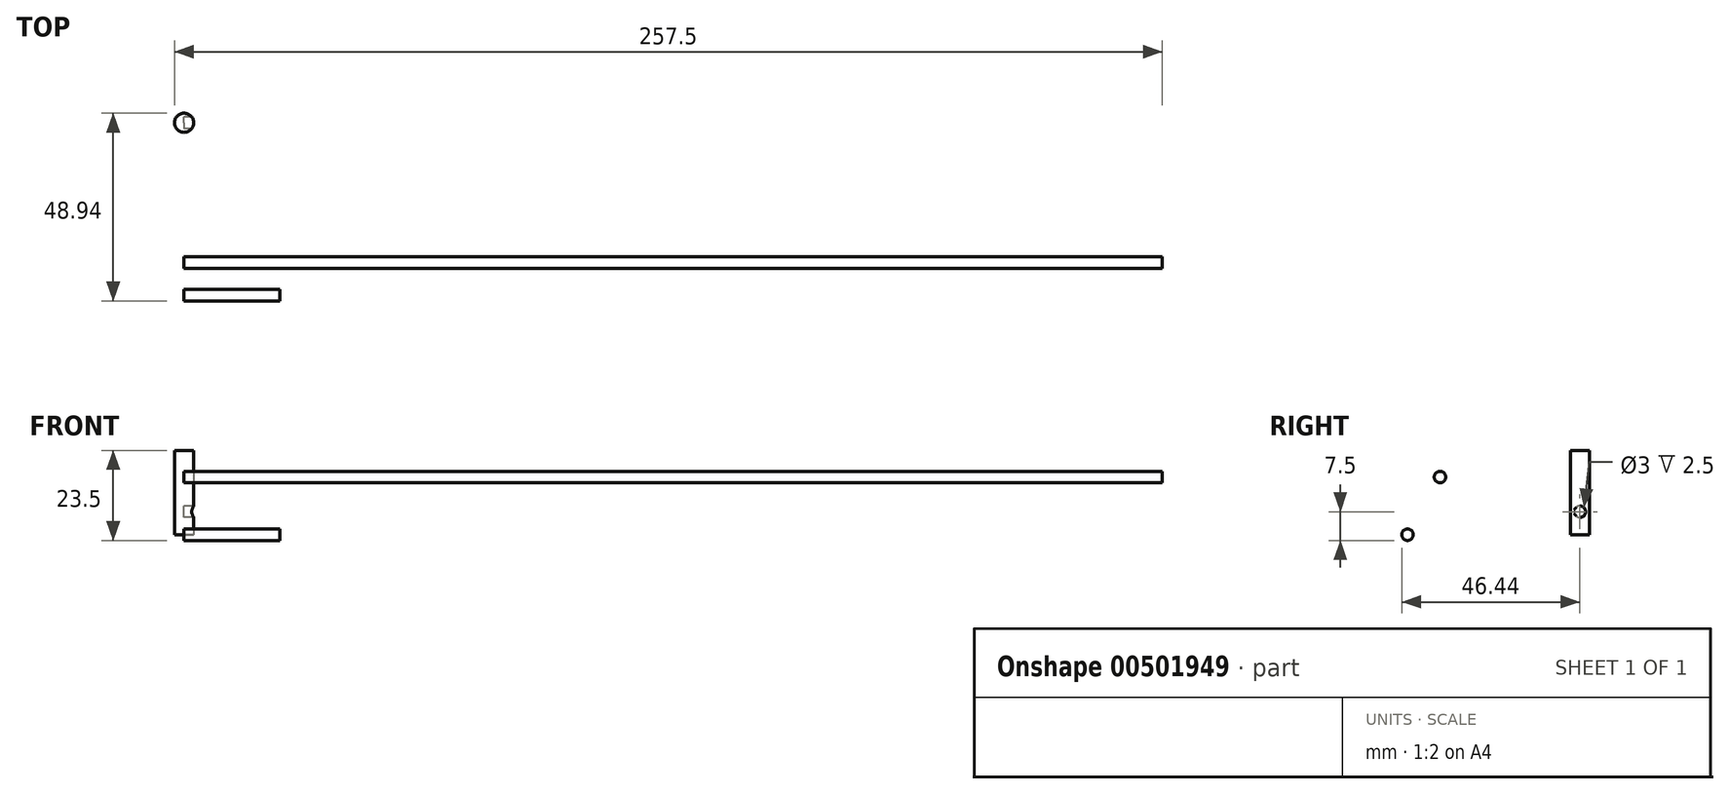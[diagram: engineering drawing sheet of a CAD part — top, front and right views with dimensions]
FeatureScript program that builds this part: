
annotation { "Feature Type Name" : "Feature", "Feature Type Description" : "" }
export const myFeature = defineFeature(function(context is Context, id is Id, definition is map)
    precondition{}
    {
        {
            var Q0;
            Q0=qCreatedBy(makeId("Top.planeOp"),FACE);
            var sketch = newSketch(context, id + "F0", { "sketchPlane" : qUnion([Q0])});
            skCircle(sketch, "E0", {"center": v(0, 0) * mm, "radius": 2.5 * mm});
            skSolve(sketch);
        }
        {
            var Q0;
            Q0 = qSketchRegion(id + "F0", true);
            extrude(context, id + "F1", {"entities" : qUnion([Q0]), "depth" : 22 * mm});
        }
        {
            var Q0;
            Q0=qCreatedBy(makeId("Right.planeOp"),FACE);
            var sketch = newSketch(context, id + "F2", { "sketchPlane" : qUnion([Q0])});
            skCircle(sketch, "E1", {"center": v(0, 6) * mm, "radius": 1.5 * mm});
            skSolve(sketch);
        }
        {
            var Q0;
            Q0 = qSketchRegion(id + "F2", true);
            extrude(context, id + "F3", {"entities" : qUnion([Q0]), "operationType" : NewBodyOperationType.REMOVE, "depth" : 25 * mm});
        }
        {
            var Q0;
            Q0=qCreatedBy(makeId("Right.planeOp"),FACE);
            var sketch = newSketch(context, id + "F4", { "sketchPlane" : qUnion([Q0])});
            skCircle(sketch, "E2", {"center": v(-36.47, 15.05) * mm, "radius": 1.5 * mm});
            skSolve(sketch);
        }
        {
            var Q0;
            Q0 = qSketchRegion(id + "F4", true);
            extrude(context, id + "F5", {"entities" : qUnion([Q0]), "depth" : 255 * mm});
        }
        {
            var Q0;
            Q0=qCreatedBy(makeId("Right.planeOp"),FACE);
            var sketch = newSketch(context, id + "F6", { "sketchPlane" : qUnion([Q0])});
            skCircle(sketch, "E3", {"center": v(-44.94, 0) * mm, "radius": 1.5 * mm});
            skSolve(sketch);
        }
        {
            var Q0;
            Q0 = qSketchRegion(id + "F6", true);
            extrude(context, id + "F7", {"entities" : qUnion([Q0]), "depth" : 25 * mm});
        }
    });
